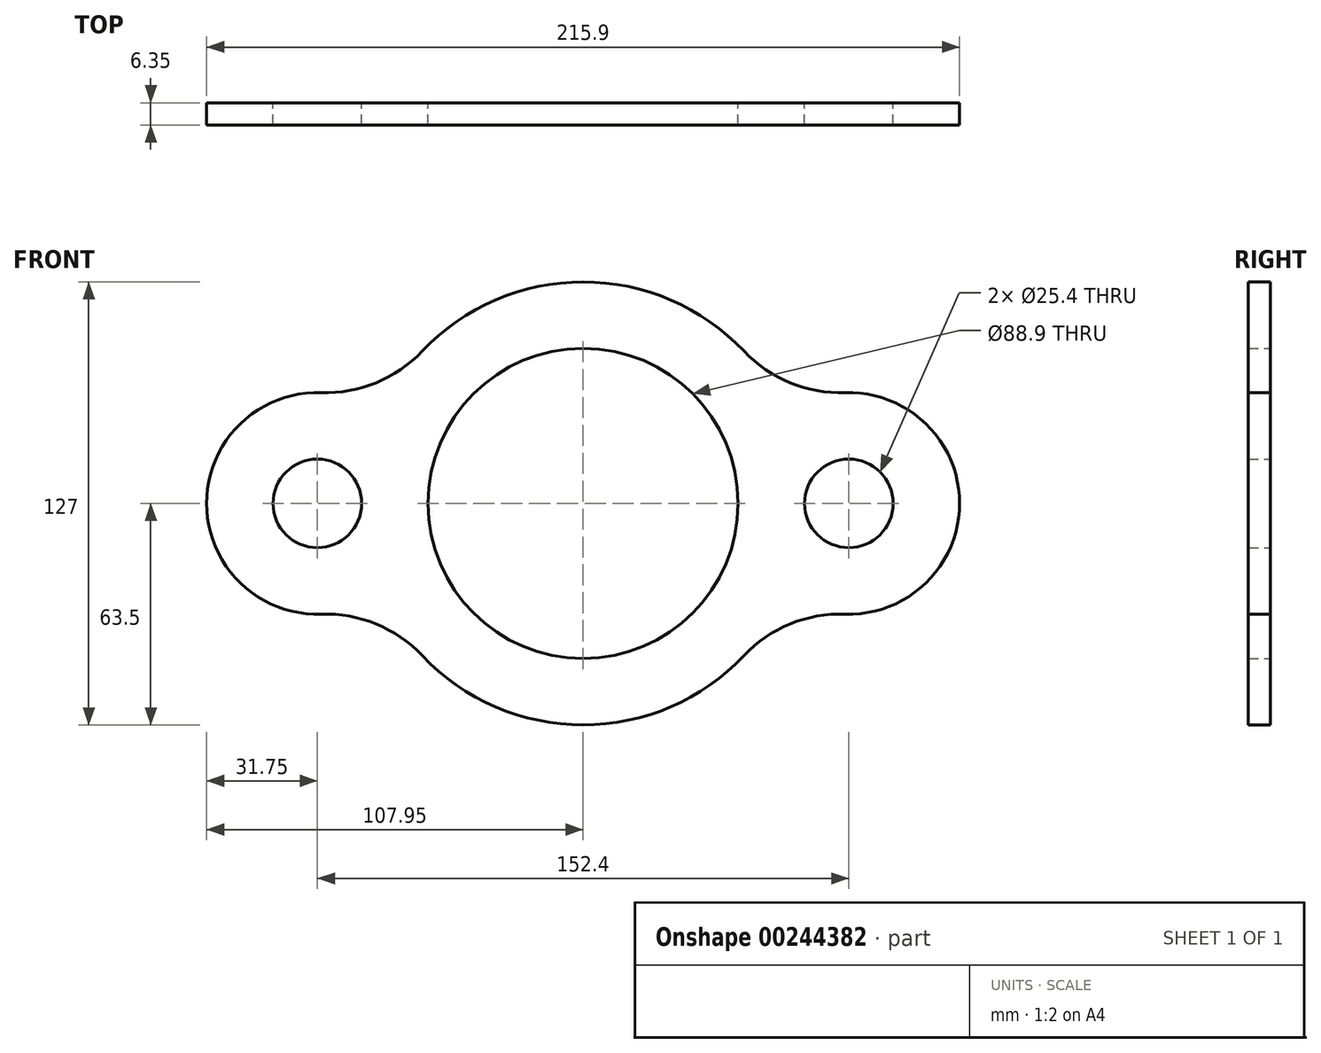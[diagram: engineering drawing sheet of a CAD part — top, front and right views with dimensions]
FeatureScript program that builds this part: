
annotation { "Feature Type Name" : "Feature", "Feature Type Description" : "" }
export const myFeature = defineFeature(function(context is Context, id is Id, definition is map)
    precondition{}
    {
        {
            var Q0;
            Q0=qCreatedBy(makeId("Front.planeOp"),FACE);
            var sketch = newSketch(context, id + "F0", { "sketchPlane" : qUnion([Q0])});
            skArc(sketch, "E0", {"start": v(-46.14, -43.63) * mm, "mid": v(0, -63.5) * mm, "end": v(46.14, -43.63) * mm});
            skArc(sketch, "E1", {"start": v(-75.12, 31.73) * mm, "mid": v(-107.95, 0) * mm, "end": v(-75.12, -31.73) * mm});
            skArc(sketch, "E2", {"start": v(75.12, -31.73) * mm, "mid": v(107.95, 0) * mm, "end": v(75.12, 31.73) * mm});
            skCircle(sketch, "E3", {"center": v(0, 0) * mm, "radius": 44.45 * mm});
            skCircle(sketch, "E4", {"center": v(-76.2, 0) * mm, "radius": 12.7 * mm});
            skCircle(sketch, "E5", {"center": v(76.2, 0) * mm, "radius": 12.7 * mm});
            skArc(sketch, "E6.trimOffspring", {"start": v(46.14, 43.63) * mm, "mid": v(0, 63.5) * mm, "end": v(-46.14, 43.63) * mm});
            skPoint(sketch, "E7.visualSharp", {"position": v(-57.94, 25.98) * mm});
            skArc(sketch, "E7.filletArc", {"start": v(-75.12, 31.73) * mm, "mid": v(-59.35, 34.56) * mm, "end": v(-46.14, 43.63) * mm});
            skPoint(sketch, "E8.visualSharp", {"position": v(-57.94, -25.98) * mm});
            skArc(sketch, "E8.filletArc", {"start": v(-46.14, -43.63) * mm, "mid": v(-59.35, -34.56) * mm, "end": v(-75.12, -31.73) * mm});
            skPoint(sketch, "E9.visualSharp", {"position": v(57.94, -25.98) * mm});
            skArc(sketch, "E9.filletArc", {"start": v(75.12, -31.73) * mm, "mid": v(59.35, -34.56) * mm, "end": v(46.14, -43.63) * mm});
            skPoint(sketch, "E10.visualSharp", {"position": v(57.94, 25.98) * mm});
            skArc(sketch, "E10.filletArc", {"start": v(46.14, 43.63) * mm, "mid": v(59.35, 34.56) * mm, "end": v(75.12, 31.73) * mm});
            skSolve(sketch);
        }
        {
            var Q0;
            Q0 = qSketchRegion(id + "F0", true);
            extrude(context, id + "F1", {"entities" : qUnion([Q0]), "depth" : 6.35 * mm});
        }
    });
